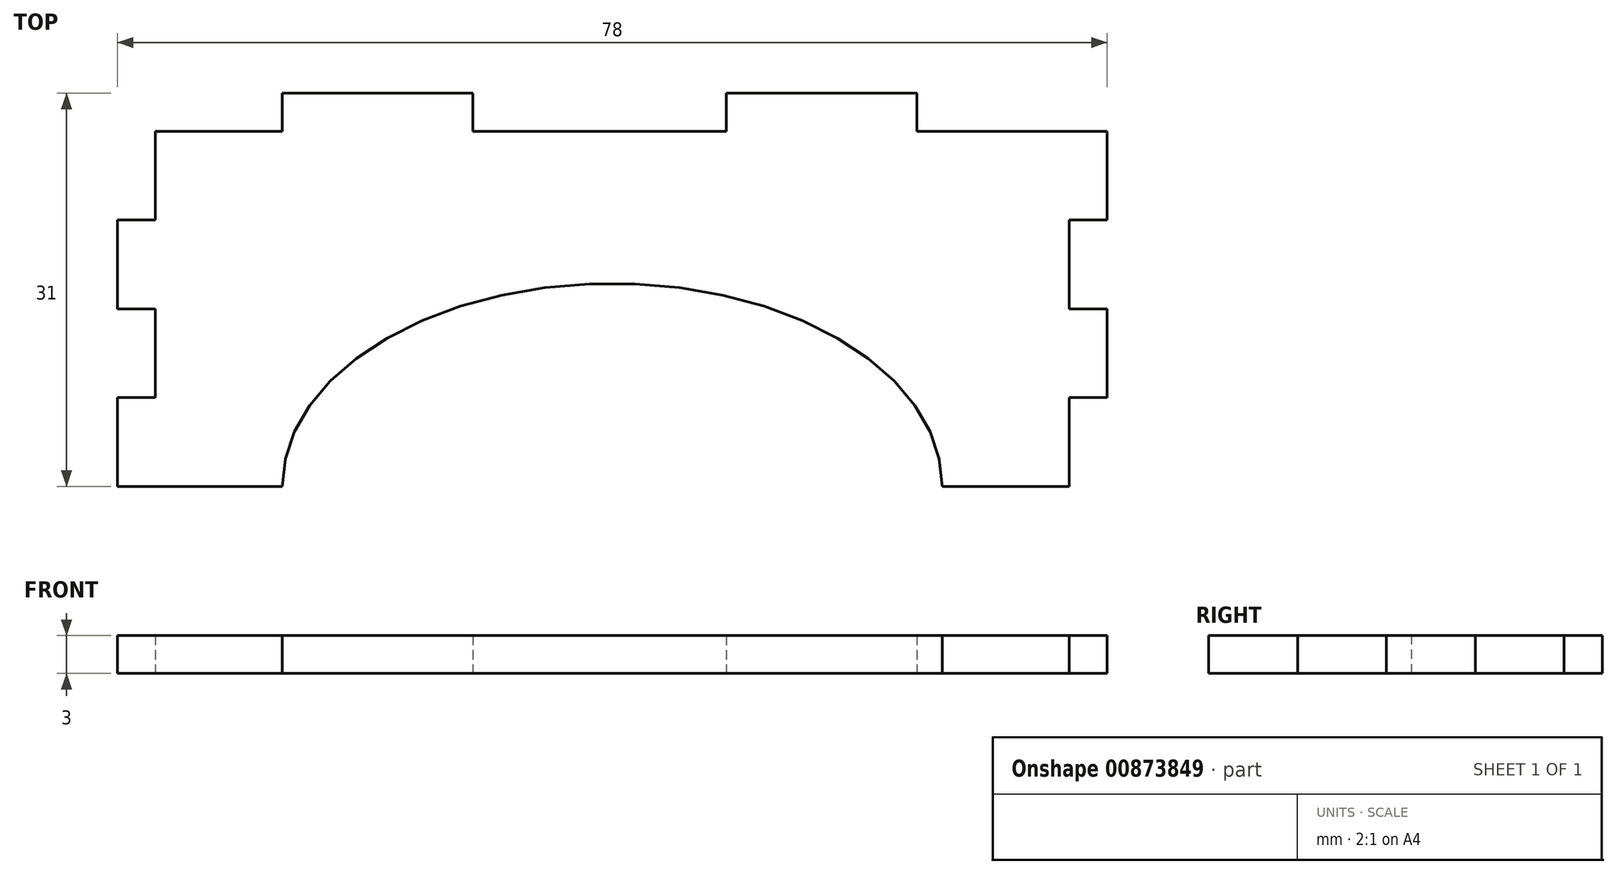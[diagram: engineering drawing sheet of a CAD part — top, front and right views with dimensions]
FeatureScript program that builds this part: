
annotation { "Feature Type Name" : "Feature", "Feature Type Description" : "" }
export const myFeature = defineFeature(function(context is Context, id is Id, definition is map)
    precondition{}
    {
        {
            var Q0;
            Q0=qCreatedBy(makeId("Top.planeOp"),FACE);
            var sketch = newSketch(context, id + "F0", { "sketchPlane" : qUnion([Q0])});
            skLineSegment(sketch, "E0.bottom", {"start": v(-36, 0) * mm, "end": v(-26, 0) * mm});
            skLineSegment(sketch, "E0.top", {"start": v(-39, -28) * mm, "end": v(-26, -28) * mm});
            skLineSegment(sketch, "E0.left", {"start": v(-39, -7) * mm, "end": v(-39, -14) * mm});
            skLineSegment(sketch, "E0.right", {"start": v(39, 0) * mm, "end": v(39, -7) * mm});
            skEllipticalArc(sketch, "E1", {});
            skLineSegment(sketch, "E2.trimOffspring", {"start": v(26, -28) * mm, "end": v(36, -28) * mm});
            skLineSegment(sketch, "E3", {"start": v(39, -7) * mm, "end": v(36, -7) * mm});
            skLineSegment(sketch, "E4", {"start": v(36, -7) * mm, "end": v(36, -14) * mm});
            skLineSegment(sketch, "E5", {"start": v(36, -14) * mm, "end": v(39, -14) * mm});
            skLineSegment(sketch, "E6", {"start": v(-36, 0) * mm, "end": v(-36, -7) * mm});
            skLineSegment(sketch, "E7", {"start": v(-36, -7) * mm, "end": v(-39, -7) * mm});
            skLineSegment(sketch, "E8.0.1.0", {"start": v(-36, -14) * mm, "end": v(-36, -21) * mm});
            skLineSegment(sketch, "E8.0.1.1", {"start": v(-36, -21) * mm, "end": v(-39, -21) * mm});
            skLineSegment(sketch, "E8.0.1.2", {"start": v(-39, -14) * mm, "end": v(-36, -14) * mm});
            skLineSegment(sketch, "E8.0.1.3", {"start": v(39, -21) * mm, "end": v(36, -21) * mm});
            skLineSegment(sketch, "E8.0.1.5", {"start": v(36, -21) * mm, "end": v(36, -28) * mm});
            skLineSegment(sketch, "E8.direction1", {"start": v(-39, -7) * mm, "end": v(-13, -7) * mm, "construction": true});
            skLineSegment(sketch, "E8.direction2", {"start": v(-39, -7) * mm, "end": v(-39, -14) * mm, "construction": true});
            skLineSegment(sketch, "E9.trimOffspring", {"start": v(-39, -21) * mm, "end": v(-39, -28) * mm});
            skLineSegment(sketch, "E10.trimOffspring", {"start": v(39, -14) * mm, "end": v(39, -21) * mm});
            skPoint(sketch, "E11.orphan", {"position": v(39, -28) * mm});
            skLineSegment(sketch, "E12", {"start": v(-26, 0) * mm, "end": v(-26, 3) * mm});
            skLineSegment(sketch, "E13", {"start": v(-26, 3) * mm, "end": v(-11, 3) * mm});
            skLineSegment(sketch, "E14", {"start": v(-11, 3) * mm, "end": v(-11, 0) * mm});
            skLineSegment(sketch, "E15", {"start": v(9, 0) * mm, "end": v(9, 3) * mm});
            skLineSegment(sketch, "E16", {"start": v(9, 3) * mm, "end": v(24, 3) * mm});
            skLineSegment(sketch, "E17", {"start": v(24, 3) * mm, "end": v(24, 0) * mm});
            skLineSegment(sketch, "E18.trimOffspring", {"start": v(24, 0) * mm, "end": v(39, 0) * mm});
            skLineSegment(sketch, "E19.trimOffspring", {"start": v(-11, 0) * mm, "end": v(9, 0) * mm});
            const initialGuessF0  = {"E1": [0, -0.028, -1, 0, 0.026, 0.016, 3.141592653589793, 0]};
            skSetInitialGuess(sketch, initialGuessF0);
            skSolve(sketch);
        }
        {
            var Q0;
            Q0 = qSketchRegion(id + "F0", true);
            extrude(context, id + "F1", {"entities" : qUnion([Q0]), "depth" : 3 * mm, "offsetDistance" : 25 * mm});
        }
    });
